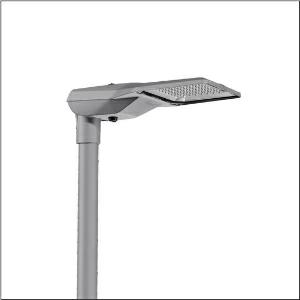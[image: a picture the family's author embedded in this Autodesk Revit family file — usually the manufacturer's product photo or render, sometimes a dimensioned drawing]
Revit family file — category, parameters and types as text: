
# Revit family: streetlight_sl_21_iq_midi___st1_0a_5xe3d61y08nb_32be
name_source: partatom
category: Lighting Fixtures
units: mm (PartAtom-declared; Revit-internal decimal feet)

## family parameters
Cut with Voids When Loaded = No
Host = Face
Light Source = No
Part Type = Normal
Room Calculation Point = No
Round Connector Dimension = Use Diameter
Shared = No

## types (1)
- --- (1 x LED, 18700 lm, 136.6 W, 2700K)
    Apparent Load = 137 VA
    CIE Flux Codes = 40 73 97 100 100
    Color Rendering = 70
    Color Temperature = 2700K
    Default Elevation = 1800 mm
    Description = Streetlight SL 21 iQ midi, mast luminaire, primary light control with lens, of PMMA, primary optical cover: cover, of toughened safety glass, transparent, light distribution: ST1.0a, light emission: direct distribution, primary light characteristic: asymmetric, installation type: post-top, side-entry, LED, High Power LED, rated luminous flux: 18.700lm, luminous efficacy: 137lm/W, light colour: 727, colour temperature: 2700K, control: pre-setting: logarithmic dimming characteristic, Street-Remote, Auto-Match, Temp-Guard, Lumen-Switch, Night-Set, Smart-Wire, Light-Fading, Desk-Remote (wireless, voltage-free reading and setting of iQ features in the workshop via application-optimized NFC function/RFID function), optimised constant luminous flux control (CLO 2.0), mains connection: 230..240V, AC, 50/60Hz, start of lifetime: 137W, end of service life: 144W, reduction: 61W, luminaire housing, of diecast aluminium, powder-coated, Siteco® metallic grey (DB 702S), corrosivity category C5 mid according to DIN EN ISO 12944, please order mast flange separately, inclination adjustable: 0°, 5°, 10°, 15°, sealing non-destructively replaceable, multi-level sealing system, length: 644mm, width: 335mm, height: 110mm, mast flange for spigot size: 42mm (side-entry): 5XC10008XM4, 60/48mm (side-entry/post-top): 5XC10108XM2, 76/60mm (side-entry/post-top): 5XC10108XM1, Smart Interface below and above, protection rating (complete): IP66, insulation class (complete): insulation class II (safety insulation), certification: CE, ENEC, ENEC+, VDE, impact resistance: IK09, permissible operating ambient temperature for outdoor applications: -40..+50°C, standard-compliant lighting for roads and squares, packaging unit: 1 piece

Light Distribution: ST1.0a
    Height = 111 mm
    Lamp = 1 x LED
    Lamp Light Flux = 18700 lm
    Lamp Power = 136.6 W
    Lamp count = 1
    Length = 644 mm
    Luminous efficacy = 137 lm/W
    Manufacturer = Siteco
    ModVariant = No
    Model = 5XE3D61Y08NB
    Number of Poles = 1
    OnlyDefault = Yes
    Power Factor = 1
    Product Name = Streetlight SL 21 iQ midi | ST1.0a
    Product group = mast luminaire | pylon top
    ProductGroupID = 6100
    Protection Class = Protection class II
    Protection Degree = IP 66
    RLX_Detail_Level = 1
    RLX_Emergency_Light_Flux = 0 lm
    RLX_Emergency_Type = 0
    RLX_Emergency_Type_DB = No
    RlxData = <blob elided: 91237 chars, md5=1e7d08cc>
    Socket = socket
    Standby Power = 0 W
    System Light Flux = 18701 lm
    System Power = 137 W
    Type Comments = factory setting: luminous flux: 100 % | dim-lin: 254 | 733 mA
    Type Image = l_1004304.jpg
    URL = http://relux.com
    VarID = @adj_082691
    Voltage = 0 V
    Weight = 0.00 kg
    Width = 336 mm

## geometry (parser evidence)
native form markers: Blend x4, Sweep x10
no freeform markers — native parametric forms only
